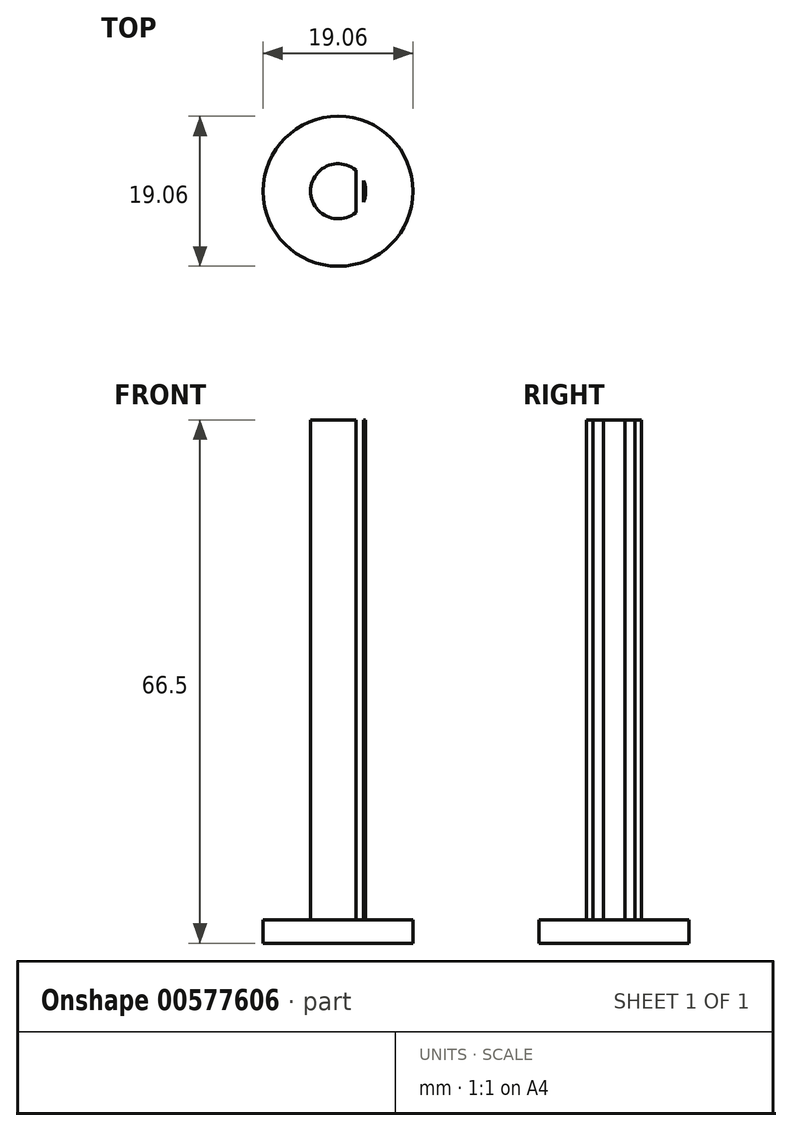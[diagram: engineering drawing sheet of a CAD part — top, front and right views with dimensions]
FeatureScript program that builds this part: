
annotation { "Feature Type Name" : "Feature", "Feature Type Description" : "" }
export const myFeature = defineFeature(function(context is Context, id is Id, definition is map)
    precondition{}
    {
        {
            var Q0;
            Q0=qCreatedBy(makeId("Top.planeOp"),FACE);
            var sketch = newSketch(context, id + "F0", { "sketchPlane" : qUnion([Q0])});
            skCircle(sketch, "E0", {"center": v(0, 0) * mm, "radius": 9.53 * mm});
            skSolve(sketch);
        }
        {
            var Q0;
            Q0=makeQuery(id+"F0.imprint","IMPRINT",FACE,{"disambiguationData":[TD([[makeQuery(id+"F0.imprint","IMPRINT",EDGE,{"derivedFrom":sQuery(id+"F0.wireOp",EDGE,"E0")}),1.0]])]});
            extrude(context, id + "F1", {"entities" : qUnion([Q0]), "depth" : 3 * mm, "offsetDistance" : 25.4 * mm});
        }
        {
            var Q0;
            Q0=makeQuery(id+"F1.opExtrude","CAP_FACE",FACE,{"disambiguationData":[OSD([sQuery(id+"F0.wireOp",EDGE,"E0")])],"isStart":false});
            var sketch = newSketch(context, id + "F2", { "sketchPlane" : qUnion([Q0])});
            skCircle(sketch, "E1", {"center": v(0, 0) * mm, "radius": 3.5 * mm});
            skSolve(sketch);
        }
        {
            var Q0;
            Q0 = qSketchRegion(id + "F2", true);
            extrude(context, id + "F3", {"entities" : qUnion([Q0]), "operationType" : NewBodyOperationType.ADD, "depth" : 63.5 * mm, "offsetDistance" : 25.4 * mm});
        }
        {
            var Q0;
            Q0=makeQuery(id+"F3.opExtrude","CAP_FACE",FACE,{"disambiguationData":[OSD([sQuery(id+"F2.wireOp",EDGE,"E1")])],"isStart":false});
            var sketch = newSketch(context, id + "F4", { "sketchPlane" : qUnion([Q0])});
            skLineSegment(sketch, "E2.bottom", {"start": v(3.22, 5.6) * mm, "end": v(2.25, 5.6) * mm});
            skLineSegment(sketch, "E2.top", {"start": v(3.22, -5.99) * mm, "end": v(2.25, -5.99) * mm});
            skLineSegment(sketch, "E2.left", {"start": v(3.22, 5.6) * mm, "end": v(3.22, -5.99) * mm});
            skLineSegment(sketch, "E2.right", {"start": v(2.25, 5.6) * mm, "end": v(2.25, -5.99) * mm});
            skSolve(sketch);
        }
        {
            var Q0;
            Q0 = qSketchRegion(id + "F4", true);
            extrude(context, id + "F5", {"entities" : qUnion([Q0]), "operationType" : NewBodyOperationType.REMOVE, "oppositeDirection" : true, "depth" : 63.5 * mm, "offsetDistance" : 25.4 * mm});
        }
    });
